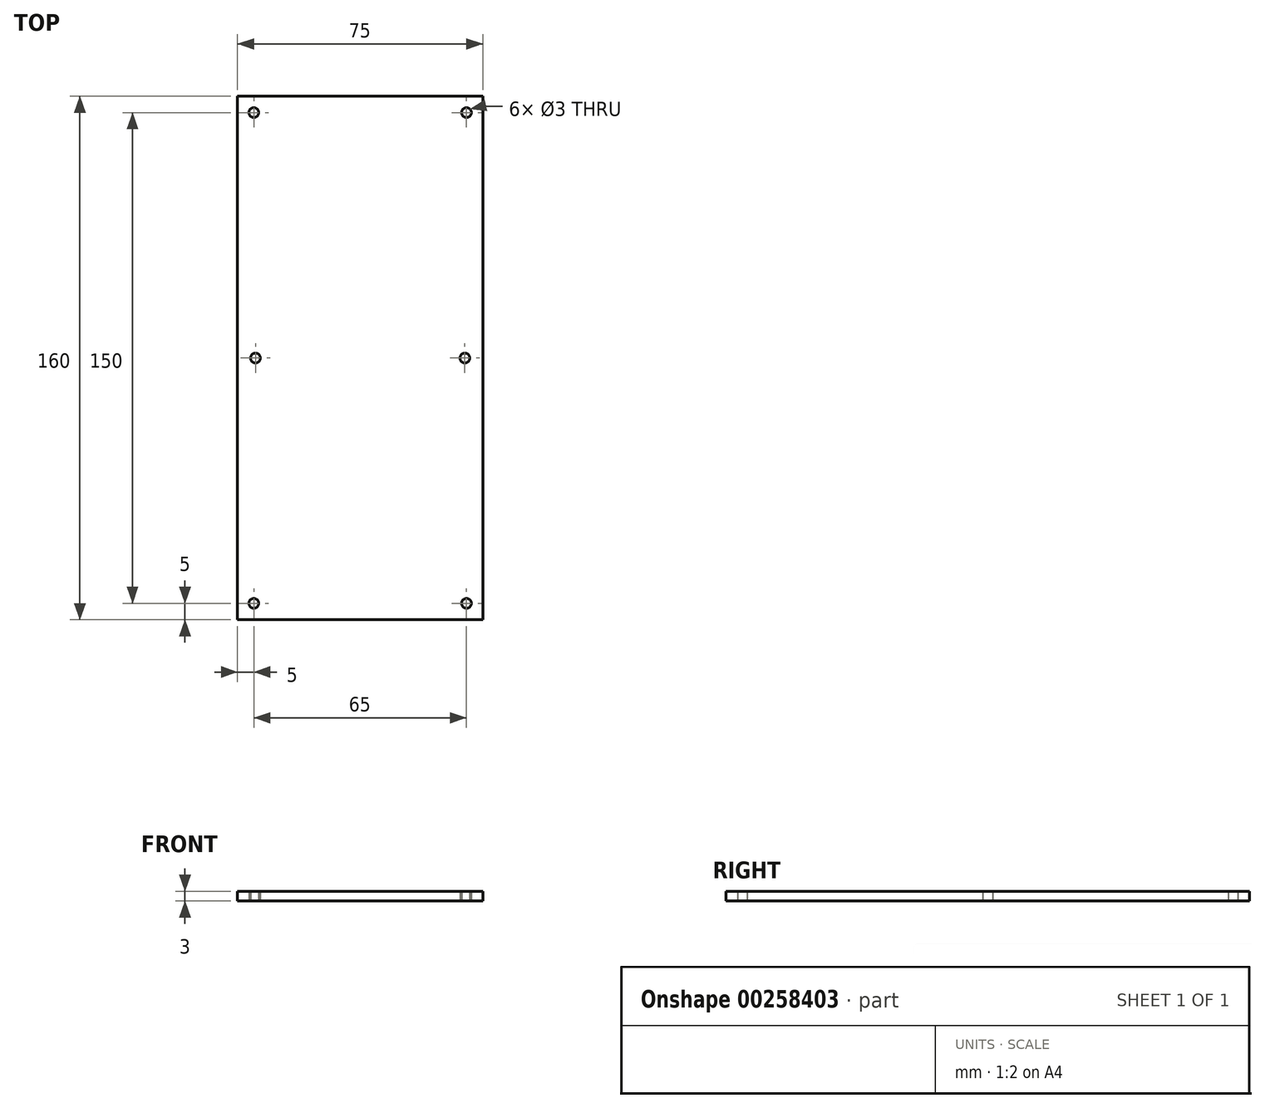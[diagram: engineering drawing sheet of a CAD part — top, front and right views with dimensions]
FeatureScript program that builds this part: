
annotation { "Feature Type Name" : "Feature", "Feature Type Description" : "" }
export const myFeature = defineFeature(function(context is Context, id is Id, definition is map)
    precondition{}
    {
        {
            var Q0;
            Q0=qCreatedBy(makeId("Top.planeOp"),FACE);
            var sketch = newSketch(context, id + "F0", { "sketchPlane" : qUnion([Q0])});
            skLineSegment(sketch, "E0.bottom", {"start": v(37.5, -80) * mm, "end": v(-37.5, -80) * mm});
            skLineSegment(sketch, "E0.top", {"start": v(37.5, 80) * mm, "end": v(-37.5, 80) * mm});
            skLineSegment(sketch, "E0.left", {"start": v(37.5, -80) * mm, "end": v(37.5, 80) * mm});
            skLineSegment(sketch, "E0.right", {"start": v(-37.5, -80) * mm, "end": v(-37.5, 80) * mm});
            skPoint(sketch, "E0.middle", {"position": v(0, 0) * mm});
            skCircle(sketch, "E1", {"center": v(-32.5, 75) * mm, "radius": 1.5 * mm});
            skCircle(sketch, "E2.MirrorC", {"center": v(32.5, 75) * mm, "radius": 1.5 * mm});
            skCircle(sketch, "E3.MirrorC", {"center": v(-32.5, -75) * mm, "radius": 1.5 * mm});
            skCircle(sketch, "E4.MirrorC", {"center": v(32.5, -75) * mm, "radius": 1.5 * mm});
            skCircle(sketch, "E5", {"center": v(-32, 0) * mm, "radius": 1.5 * mm});
            skCircle(sketch, "E6.MirrorC", {"center": v(32, 0) * mm, "radius": 1.5 * mm});
            skSolve(sketch);
        }
        {
            var Q0;
            Q0=makeQuery(id+"F0.imprint","IMPRINT",FACE,{"disambiguationData":[TD([[makeQuery(id+"F0.imprint","IMPRINT",EDGE,{"derivedFrom":sQuery(id+"F0.wireOp",EDGE,"E0.bottom")}),-1.0]])]});
            extrude(context, id + "F1", {"entities" : qUnion([Q0]), "depth" : 3 * mm});
        }
    });
